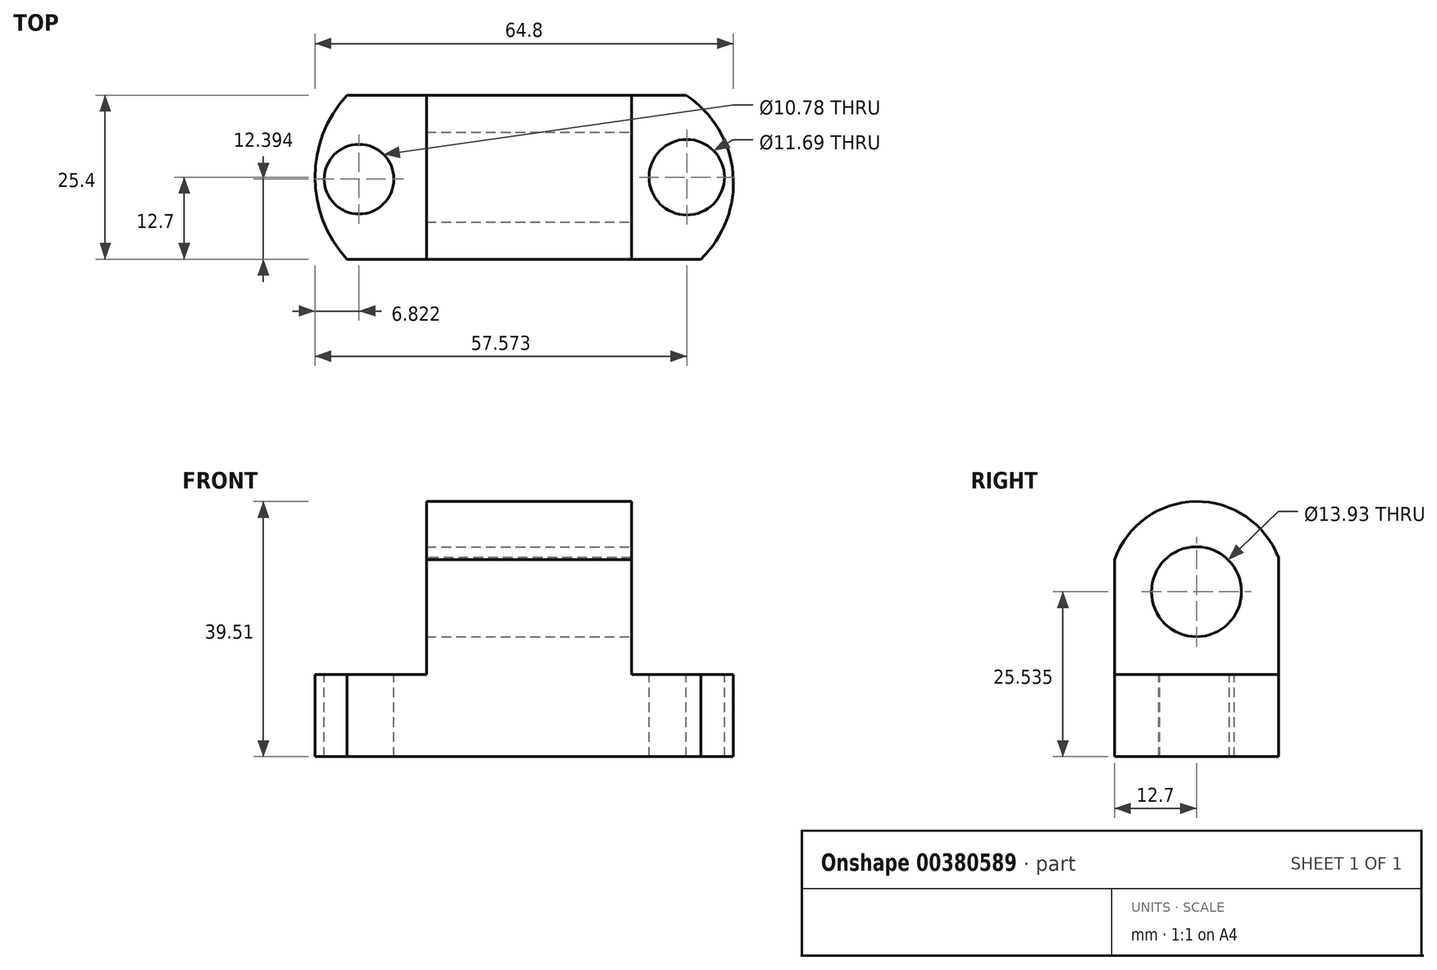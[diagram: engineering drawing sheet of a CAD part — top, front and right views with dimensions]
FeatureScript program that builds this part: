
annotation { "Feature Type Name" : "Feature", "Feature Type Description" : "" }
export const myFeature = defineFeature(function(context is Context, id is Id, definition is map)
    precondition{}
    {
        {
            var Q0;
            Q0=qCreatedBy(makeId("Front.planeOp"),FACE);
            var sketch = newSketch(context, id + "F0", { "sketchPlane" : qUnion([Q0])});
            skLineSegment(sketch, "E0", {"start": v(0, 0) * mm, "end": v(0, 12.7) * mm});
            skLineSegment(sketch, "E1", {"start": v(0, 12.7) * mm, "end": v(-16.9, 12.7) * mm});
            skLineSegment(sketch, "E2", {"start": v(-16.9, 40.55) * mm, "end": v(-16.9, 12.7) * mm});
            skLineSegment(sketch, "E3", {"start": v(-16.9, 40.55) * mm, "end": v(-48.66, 40.55) * mm});
            skLineSegment(sketch, "E4", {"start": v(-48.66, 40.55) * mm, "end": v(-48.66, 12.7) * mm});
            skLineSegment(sketch, "E5", {"start": v(-48.66, 12.7) * mm, "end": v(-67.63, 12.7) * mm});
            skLineSegment(sketch, "E6", {"start": v(-67.63, 12.7) * mm, "end": v(-67.63, 0) * mm});
            skLineSegment(sketch, "E7", {"start": v(-67.63, 0) * mm, "end": v(0, 0) * mm});
            skSolve(sketch);
        }
        {
            var Q0;
            Q0=makeQuery(id+"F0.imprint","IMPRINT",FACE,{"disambiguationData":[TD([[makeQuery(id+"F0.imprint","IMPRINT",EDGE,{"derivedFrom":sQuery(id+"F0.wireOp",EDGE,"E0")}),1.0]])]});
            extrude(context, id + "F1", {"entities" : qUnion([Q0]), "depth" : 25.4 * mm});
        }
        {
            var Q0;
            Q0=makeQuery(id+"F1.opExtrude","SWEPT_FACE",FACE,{"disambiguationData":[OSD([sQuery(id+"F0.wireOp",EDGE,"E2")])]});
            var sketch = newSketch(context, id + "F2", { "sketchPlane" : qUnion([Q0])});
            skCircle(sketch, "E8", {"center": v(-12.7, 25.54) * mm, "radius": 6.96 * mm});
            skPoint(sketch, "E8.centerSnap0", {"position": v(-12.7, 12.7) * mm});
            skSolve(sketch);
        }
        {
            var Q0;
            Q0=makeQuery(id+"F2.imprint","IMPRINT",FACE,{"disambiguationData":[TD([[makeQuery(id+"F2.imprint","IMPRINT",EDGE,{"derivedFrom":sQuery(id+"F2.wireOp",EDGE,"E8")}),1.0]])]});
            extrude(context, id + "F3", {"entities" : qUnion([Q0]), "operationType" : NewBodyOperationType.REMOVE, "oppositeDirection" : true, "depth" : 31.75 * mm});
        }
        {
            var Q0;
            Q0=makeQuery(id+"F1.opExtrude","SWEPT_FACE",FACE,{"disambiguationData":[OSD([sQuery(id+"F0.wireOp",EDGE,"E5")])]});
            var sketch = newSketch(context, id + "F4", { "sketchPlane" : qUnion([Q0])});
            skCircle(sketch, "E9", {"center": v(-59.1, -13) * mm, "radius": 5.4 * mm});
            skSolve(sketch);
        }
        {
            var Q0;
            Q0=makeQuery(id+"F4.imprint","IMPRINT",FACE,{"disambiguationData":[TD([[makeQuery(id+"F4.imprint","IMPRINT",EDGE,{"derivedFrom":sQuery(id+"F4.wireOp",EDGE,"E9")}),1.0]])]});
            extrude(context, id + "F5", {"entities" : qUnion([Q0]), "operationType" : NewBodyOperationType.REMOVE, "oppositeDirection" : true, "depth" : 12.7 * mm});
        }
        {
            var Q0;
            Q0=makeQuery(id+"F1.opExtrude","SWEPT_FACE",FACE,{"disambiguationData":[OSD([sQuery(id+"F0.wireOp",EDGE,"E1")])]});
            var sketch = newSketch(context, id + "F6", { "sketchPlane" : qUnion([Q0])});
            skCircle(sketch, "E10", {"center": v(-8.36, -12.7) * mm, "radius": 5.84 * mm});
            skSolve(sketch);
        }
        {
            var Q0;
            Q0=makeQuery(id+"F6.imprint","IMPRINT",FACE,{"disambiguationData":[TD([[makeQuery(id+"F6.imprint","IMPRINT",EDGE,{"derivedFrom":sQuery(id+"F6.wireOp",EDGE,"E10")}),1.0]])]});
            extrude(context, id + "F7", {"entities" : qUnion([Q0]), "operationType" : NewBodyOperationType.REMOVE, "oppositeDirection" : true, "depth" : 12.7 * mm});
        }
        {
            var Q0;
            Q0=makeQuery(id+"F1.opExtrude","SWEPT_FACE",FACE,{"disambiguationData":[OSD([sQuery(id+"F0.wireOp",EDGE,"E1")])]});
            var sketch = newSketch(context, id + "F8", { "sketchPlane" : qUnion([Q0])});
            skArc(sketch, "E11", {"start": v(-6.2, -25.4) * mm, "mid": v(-1.2, -12.15) * mm, "end": v(-8.45, 0) * mm});
            skSolve(sketch);
        }
        {
            var Q0;
            {var subQ0=sQuery(id+"F8.wireOp",EDGE,"E11");Q0=makeQuery(id+"F8.imprint","IMPRINT",FACE,{"disambiguationData":[TD([[makeQuery(id+"F8.imprint","IMPRINT",EDGE,{"derivedFrom":subQ0}),-1.0]])]});}
            extrude(context, id + "F9", {"entities" : qUnion([Q0]), "operationType" : NewBodyOperationType.REMOVE, "oppositeDirection" : true, "depth" : 25.4 * mm});
        }
        {
            var Q0;
            Q0=makeQuery(id+"F1.opExtrude","SWEPT_FACE",FACE,{"disambiguationData":[OSD([sQuery(id+"F0.wireOp",EDGE,"E5")])]});
            var sketch = newSketch(context, id + "F10", { "sketchPlane" : qUnion([Q0])});
            skArc(sketch, "E12", {"start": v(-60.97, 0) * mm, "mid": v(-65.93, -12.7) * mm, "end": v(-60.97, -25.4) * mm});
            skSolve(sketch);
        }
        {
            var Q0;
            {var subQ0=sQuery(id+"F10.wireOp",EDGE,"E12");Q0=makeQuery(id+"F10.imprint","IMPRINT",FACE,{"disambiguationData":[TD([[makeQuery(id+"F10.imprint","IMPRINT",EDGE,{"derivedFrom":subQ0}),-1.0]])]});}
            extrude(context, id + "F11", {"entities" : qUnion([Q0]), "operationType" : NewBodyOperationType.REMOVE, "oppositeDirection" : true, "depth" : 25.4 * mm});
        }
        {
            var Q0;
            Q0=makeQuery(id+"F1.opExtrude","SWEPT_FACE",FACE,{"disambiguationData":[OSD([sQuery(id+"F0.wireOp",EDGE,"E4")])]});
            var sketch = newSketch(context, id + "F12", { "sketchPlane" : qUnion([Q0])});
            skArc(sketch, "E13", {"start": v(25.4, 30.49) * mm, "mid": v(12.8, 39.5) * mm, "end": v(0, 30.8) * mm});
            skSolve(sketch);
        }
        {
            var Q0;
            {var subQ0=sQuery(id+"F12.wireOp",EDGE,"E13");Q0=makeQuery(id+"F12.imprint","IMPRINT",FACE,{"disambiguationData":[TD([[makeQuery(id+"F12.imprint","IMPRINT",EDGE,{"derivedFrom":subQ0}),-1.0]])]});}
            extrude(context, id + "F13", {"entities" : qUnion([Q0]), "operationType" : NewBodyOperationType.REMOVE, "oppositeDirection" : true, "depth" : 38.1 * mm});
        }
    });
